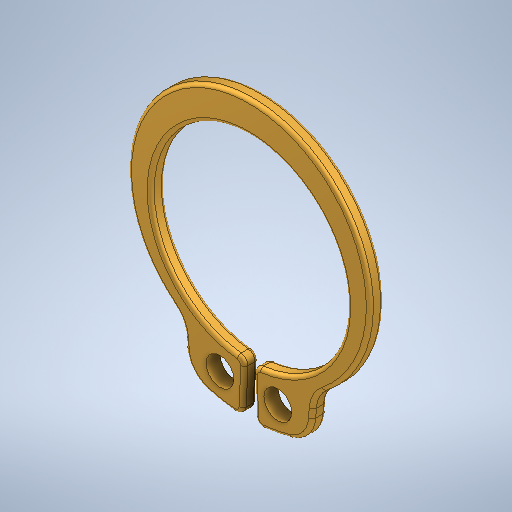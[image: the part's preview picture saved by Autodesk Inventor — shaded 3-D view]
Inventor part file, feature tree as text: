
AUTODESK INVENTOR PART (.ipt)
format: ipt  version: 2025 (Build 290162000, 162)  size: 349,184 bytes
history: native  units: in
note: dims shown in document units (in); Inventor stores cm internally (conversion verified against a paired STEP export)
features: fillet x1
ambient origin geometry x8: Origin, YZ Plane, XZ Plane, XY Plane, X Axis, Y Axis, Z Axis, Center Point
bodies: Solid1 (feature_tree)
feature tree (1):
  fillet  "Fillet3"  [1 undecoded]
note: 1 required parameter value undecoded (feature->parameter linkage not recoverable at this tier; creation-order binding heuristic only, values carry confidence <= 0.55)
